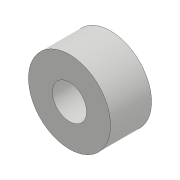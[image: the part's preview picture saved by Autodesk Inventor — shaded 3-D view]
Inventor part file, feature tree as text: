
AUTODESK INVENTOR PART (.ipt)
format: ipt  version: 2018 (Build 220112000, 112)  size: 81,408 bytes
history: native  units: mm
features: extrude x1, sketch x1
ambient origin geometry x8: Origin, YZ Plane, XZ Plane, XY Plane, X Axis, Y Axis, Z Axis, Center Point
bodies: Solid1 (feature_tree)
feature tree (2):
  extrude  "Extrusion1"  Depth=3.0mm
  sketch  "Sketch1"  dims[d0=2.5mm d1=6.0mm d2=3.0mm d3=0.0mm]
